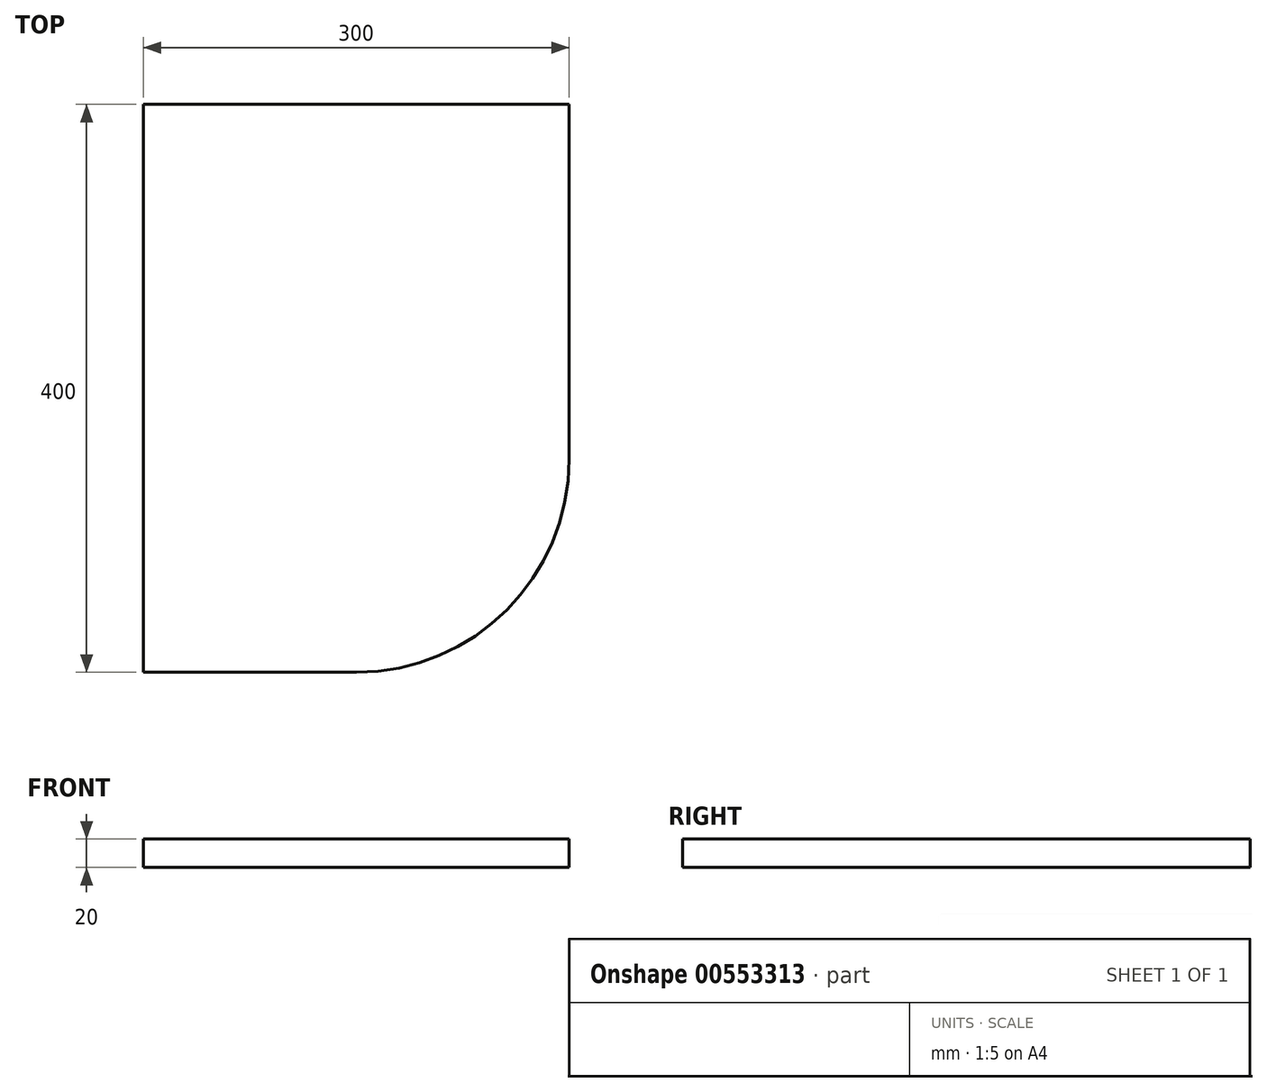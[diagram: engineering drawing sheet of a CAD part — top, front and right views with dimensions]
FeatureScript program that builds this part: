
annotation { "Feature Type Name" : "Feature", "Feature Type Description" : "" }
export const myFeature = defineFeature(function(context is Context, id is Id, definition is map)
    precondition{}
    {
        {
            var Q0;
            Q0=qCreatedBy(makeId("Top.planeOp"),FACE);
            var sketch = newSketch(context, id + "F0", { "sketchPlane" : qUnion([Q0])});
            skLineSegment(sketch, "E0.bottom", {"start": v(150, -200) * mm, "end": v(-150, -200) * mm});
            skLineSegment(sketch, "E0.top", {"start": v(150, 200) * mm, "end": v(-150, 200) * mm});
            skLineSegment(sketch, "E0.left", {"start": v(150, -200) * mm, "end": v(150, 200) * mm});
            skLineSegment(sketch, "E0.right", {"start": v(-150, -200) * mm, "end": v(-150, 200) * mm});
            skPoint(sketch, "E0.middle", {"position": v(0, 0) * mm});
            skSolve(sketch);
        }
        {
            var Q0;
            Q0=makeQuery(id+"F0.imprint","IMPRINT",FACE,{"disambiguationData":[TD([[makeQuery(id+"F0.imprint","IMPRINT",EDGE,{"derivedFrom":sQuery(id+"F0.wireOp",EDGE,"E0.bottom")}),-1.0]])]});
            extrude(context, id + "F1", {"entities" : qUnion([Q0]), "depth" : 20 * mm, "offsetDistance" : 25 * mm});
        }
        {
            var Q0;
            Q0=makeQuery(id+"F1.opExtrude","SWEPT_EDGE",EDGE,{"disambiguationData":[OSD([sQuery(id+"F0.wireOp",EDGE,"E0.bottom"),sQuery(id+"F0.wireOp",EDGE,"E0.left")])]});
            fillet(context, id + "F2", {"entities" : qUnion([Q0]), "radius" : 150 * mm, "tangentPropagation" : true, "defaultsChanged" : true, "vertexSettings" : [], "allowEdgeOverflow" : false});
        }
    });
